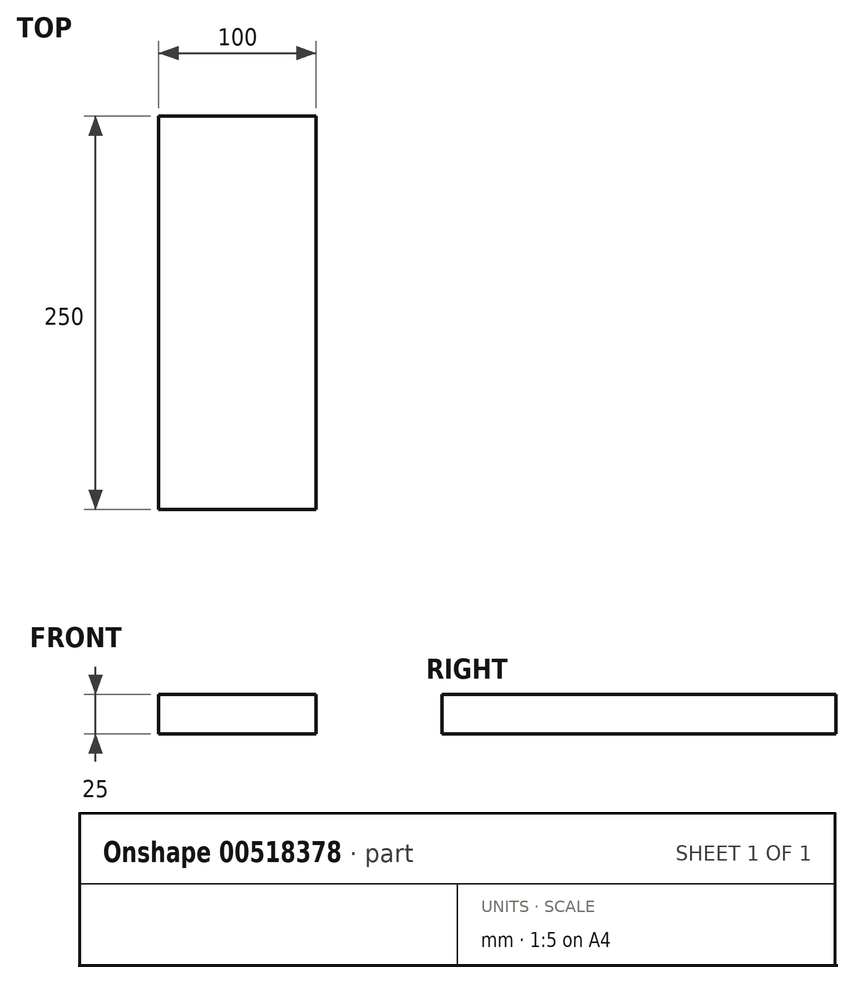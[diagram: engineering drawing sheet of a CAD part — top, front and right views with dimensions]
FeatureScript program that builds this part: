
annotation { "Feature Type Name" : "Feature", "Feature Type Description" : "" }
export const myFeature = defineFeature(function(context is Context, id is Id, definition is map)
    precondition{}
    {
        {
            var Q0;
            Q0=qCreatedBy(makeId("Top.planeOp"),FACE);
            var sketch = newSketch(context, id + "F0", { "sketchPlane" : qUnion([Q0])});
            skLineSegment(sketch, "E0.bottom", {"start": v(50, -125) * mm, "end": v(-50, -125) * mm});
            skLineSegment(sketch, "E0.top", {"start": v(50, 125) * mm, "end": v(-50, 125) * mm});
            skLineSegment(sketch, "E0.left", {"start": v(50, -125) * mm, "end": v(50, 125) * mm});
            skLineSegment(sketch, "E0.right", {"start": v(-50, -125) * mm, "end": v(-50, 125) * mm});
            skPoint(sketch, "E0.middle", {"position": v(0, 0) * mm});
            skSolve(sketch);
        }
        {
            var Q0;
            Q0=qSketchRegion(id+"F0",true);
            extrude(context, id + "F1", {"entities" : qUnion([Q0]), "depth" : 25 * mm, "offsetDistance" : 25 * mm});
        }
    });
